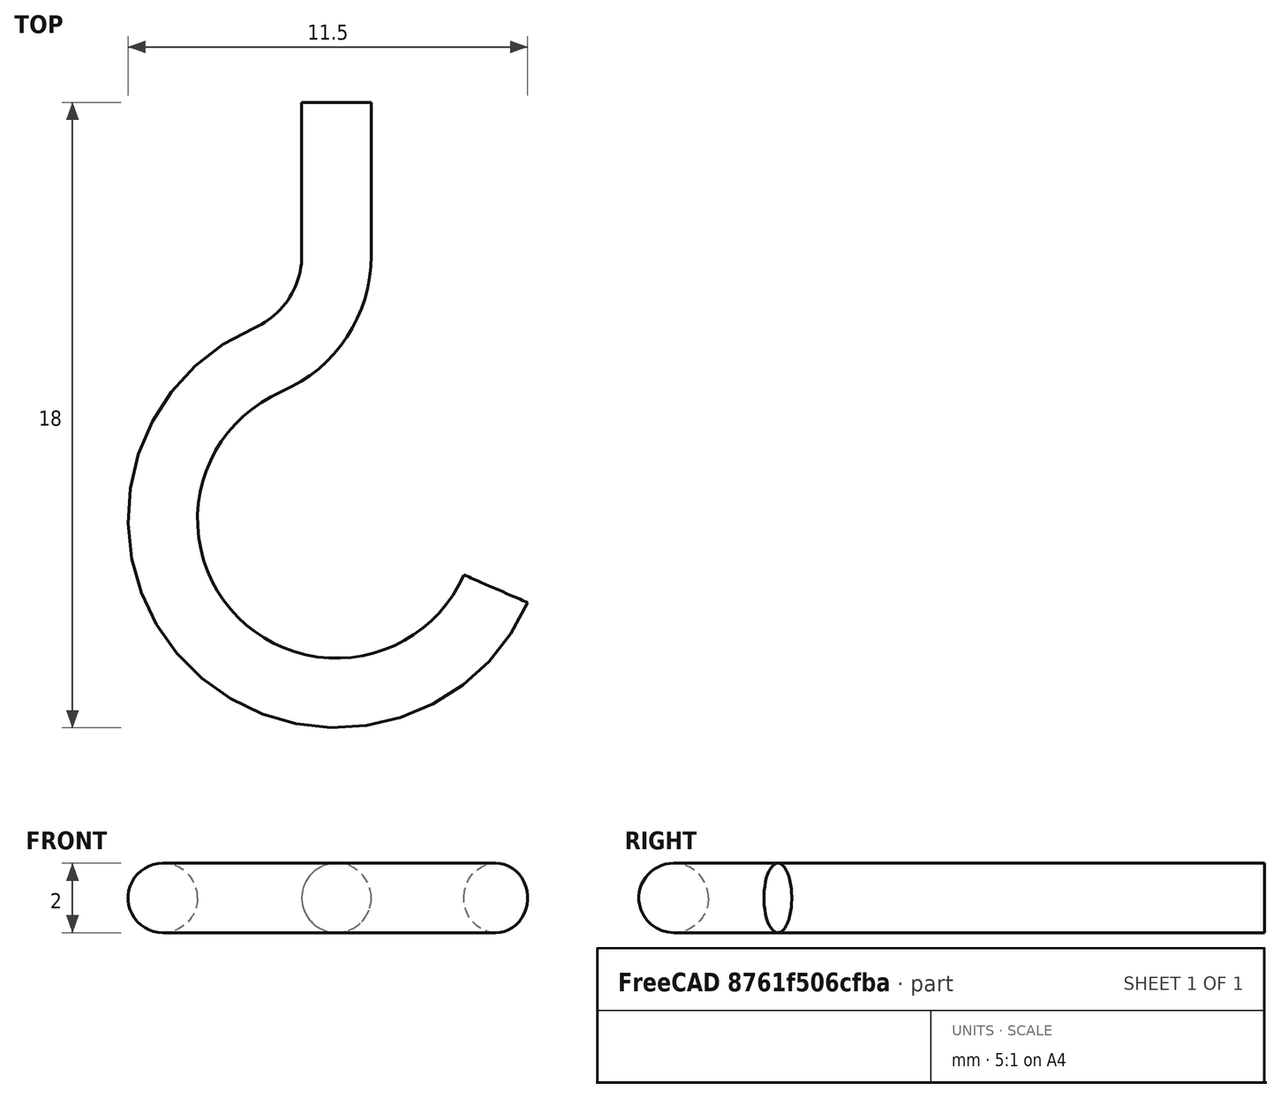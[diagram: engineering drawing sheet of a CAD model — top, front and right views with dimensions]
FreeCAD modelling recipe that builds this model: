
FCSTD DOCUMENT  (FreeCAD 0.18.4R)
Label: hook2
License: All rights reserved
LicenseURL: http://en.wikipedia.org/wiki/All_rights_reserved
objects: Sketcher::SketchObject×2, PartDesign::AdditivePipe×1, PartDesign::Body×1
note: 5 computed .brp shape members not serialized (recipe doc carries the construction recipe); baked Part::Feature solids carry a one-line shape summary decoded from their .brp

FEATURE [Sketcher::SketchObject] Sketch
  MapMode = 5
  Support = -> [XY_Plane]
  sketch-geometry (3):
    g0: ArcOfCircle CenterX=0 CenterY=0 CenterZ=0 NormalX=0 NormalY=0 NormalZ=1 AngleXU=0 Radius=5 StartAngle=1.97696 EndAngle=5.87167
    g1: LineSegment StartX=0 StartY=7.59321 StartZ=0 EndX=0 EndY=12 EndZ=0
    g2: ArcOfCircle CenterX=-3.26569 CenterY=7.59321 CenterZ=0 NormalX=0 NormalY=0 NormalZ=1 AngleXU=0 Radius=3.26569 StartAngle=5.11855 EndAngle=6.28319
  constraints (9):
    c: Coincident(g0,g-1)
    c: PointOnObject(g1,g-2)
    c: Vertical(g1)
    c: Tangent(g0,g2) = 1.5708
    c: Tangent(g1,g2) = -1.5708
    c: Radius(g0) = 5
    c: DistanceY(g0,g0) = 2
    c: DistanceY(g0,g1) = 12
    c: DistanceY(g0,g1) = 3
FEATURE [Sketcher::SketchObject] Sketch001
  AttachmentOffset = pos=(0,0,-12) rot=(0,0,1;0rad)
  MapMode = 5
  Placement = pos=(0,12,2.7e-15) rot=(1,0,0;1.5708rad)
  Support = -> [XZ_Plane]
  sketch-geometry (1):
    g0: Circle CenterX=0 CenterY=0 CenterZ=0 NormalX=0 NormalY=0 NormalZ=1 AngleXU=0 Radius=1
  constraints (2):
    c: Coincident(g0,g-1)
    c: Radius(g0) = 1
FEATURE [PartDesign::AdditivePipe] AdditivePipe
  AuxilleryCurvelinear = true
  AuxillerySpineTangent = false
  Binormal = (0,0,0)
  Mode = 0
  Placement = pos=(0,0,0) rot=(1,0,0;1.5708rad)
  Profile = -> Sketch001
  Spine = -> Sketch
  SpineTangent = false
  Transformation = 0
  Transition = 0
FEATURE [PartDesign::Body] Body
  Group = -> [Sketch,Sketch001,AdditivePipe]
  Origin = -> Origin
  Tip = -> AdditivePipe
